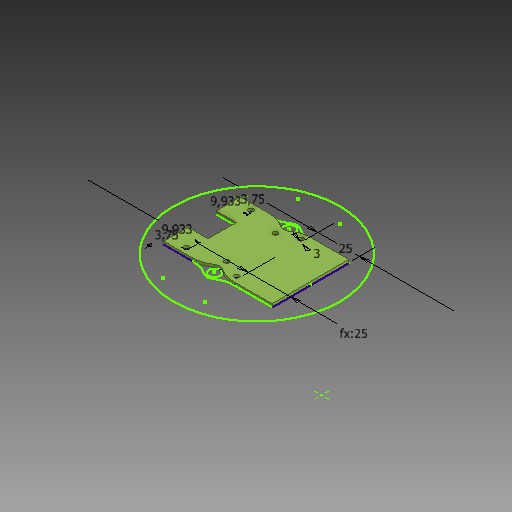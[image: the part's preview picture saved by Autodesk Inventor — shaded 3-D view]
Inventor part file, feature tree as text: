
AUTODESK INVENTOR PART (.ipt)
format: ipt  version: 2020 (Build 240168000, 168)  size: 161,792 bytes
history: native  units: mm
features: other x2, sketch x2, extrude x1
ambient origin geometry x8: Origin, YZ Plane, XZ Plane, XY Plane, X Axis, Y Axis, Z Axis, Center Point
bodies: Body1 (feature_tree)
feature tree (5):
  other  "openMV_board"
  other  "Твердое тело1"
  sketch  "Эскиз1"
  extrude  "Выдавливание1"  Depth=35.573mm
  sketch  "Эскиз2"
